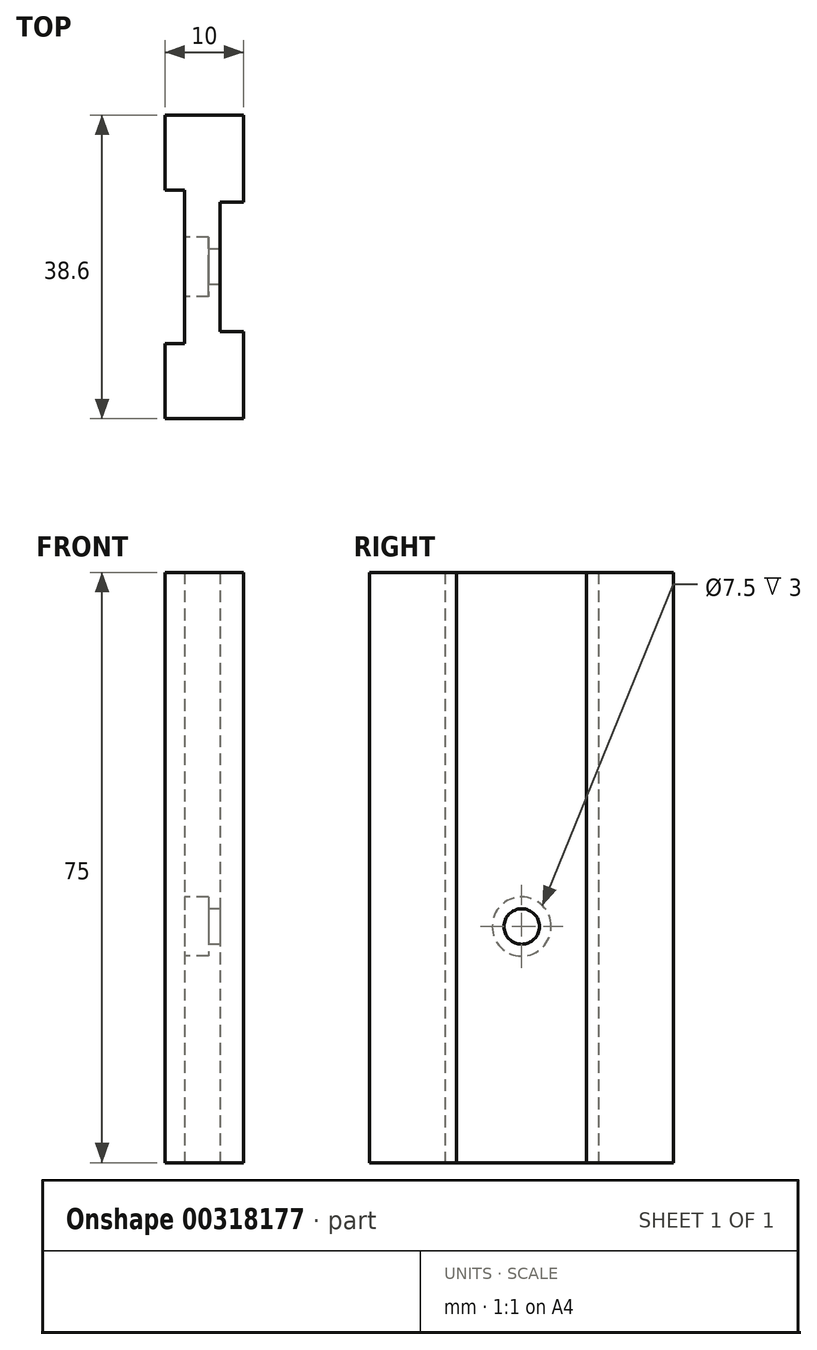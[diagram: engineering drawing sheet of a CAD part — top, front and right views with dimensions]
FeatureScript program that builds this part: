
annotation { "Feature Type Name" : "Feature", "Feature Type Description" : "" }
export const myFeature = defineFeature(function(context is Context, id is Id, definition is map)
    precondition{}
    {
        {
            var Q0;
            Q0=qCreatedBy(makeId("Top.planeOp"),FACE);
            var sketch = newSketch(context, id + "F0", { "sketchPlane" : qUnion([Q0])});
            skLineSegment(sketch, "E0.bottom", {"start": v(0, 0) * mm, "end": v(10, 0) * mm});
            skLineSegment(sketch, "E0.top", {"start": v(0, 38.6) * mm, "end": v(10, 38.6) * mm});
            skLineSegment(sketch, "E0.left", {"start": v(0, 0) * mm, "end": v(0, 9.55) * mm});
            skLineSegment(sketch, "E0.right", {"start": v(10, 0) * mm, "end": v(10, 11.05) * mm});
            skLineSegment(sketch, "E1.bottom", {"start": v(10, 11.05) * mm, "end": v(7, 11.05) * mm});
            skLineSegment(sketch, "E1.top", {"start": v(10, 27.55) * mm, "end": v(7, 27.55) * mm});
            skLineSegment(sketch, "E1.right", {"start": v(7, 11.05) * mm, "end": v(7, 27.55) * mm});
            skLineSegment(sketch, "E2.trimOffspring", {"start": v(10, 27.55) * mm, "end": v(10, 38.6) * mm});
            skLineSegment(sketch, "E3.bottom", {"start": v(0, 29.05) * mm, "end": v(2.5, 29.05) * mm});
            skLineSegment(sketch, "E3.top", {"start": v(0, 9.55) * mm, "end": v(2.5, 9.55) * mm});
            skLineSegment(sketch, "E3.right", {"start": v(2.5, 29.05) * mm, "end": v(2.5, 9.55) * mm});
            skLineSegment(sketch, "E4.trimOffspring", {"start": v(0, 29.05) * mm, "end": v(0, 38.6) * mm});
            skSolve(sketch);
        }
        {
            var Q0;
            Q0=makeQuery(id+"F0.imprint","IMPRINT",FACE,{"disambiguationData":[TD([[makeQuery(id+"F0.imprint","IMPRINT",EDGE,{"derivedFrom":sQuery(id+"F0.wireOp",EDGE,"E0.bottom")}),1.0]])]});
            extrude(context, id + "F1", {"entities" : qUnion([Q0]), "depth" : 75 * mm});
        }
        {
            var Q0;
            Q0=makeQuery(id+"F1.opExtrude","SWEPT_FACE",FACE,{"disambiguationData":[OSD([sQuery(id+"F0.wireOp",EDGE,"E3.right")])]});
            var sketch = newSketch(context, id + "F2", { "sketchPlane" : qUnion([Q0])});
            skLineSegment(sketch, "E5", {"start": v(-19.3, 0) * mm, "end": v(-19.3, 30) * mm, "construction": true});
            skSolve(sketch);
        }
        {
            var Q0;
            Q0=sQuery(id+"F2.wireOp",VERTEX,"E5.end");
            var Q1;
            Q1=makeQuery(id+"F1.opExtrude","SWEPT_BODY",BODY,{"disambiguationData":[OSD([sQuery(id+"F0.wireOp",EDGE,"E0.bottom"),sQuery(id+"F0.wireOp",EDGE,"E0.top"),sQuery(id+"F0.wireOp",EDGE,"E0.left"),sQuery(id+"F0.wireOp",EDGE,"E0.right"),sQuery(id+"F0.wireOp",EDGE,"E1.bottom"),sQuery(id+"F0.wireOp",EDGE,"E1.top"),sQuery(id+"F0.wireOp",EDGE,"E1.right"),sQuery(id+"F0.wireOp",EDGE,"E2.trimOffspring")])]});
            hole(context, id + "F3", {"style" : HoleStyle.C_BORE, "endStyle" : HoleEndStyle.THROUGH, "holeDiameter" : 4.5 * mm, "cBoreDiameter" : 7.5 * mm, "cBoreDepth" : 3 * mm, "tappedDepth" : 12 * mm, "tapClearance" : 3, "locations" : qUnion([Q0]), "scope" : qUnion([Q1])});
        }
    });
